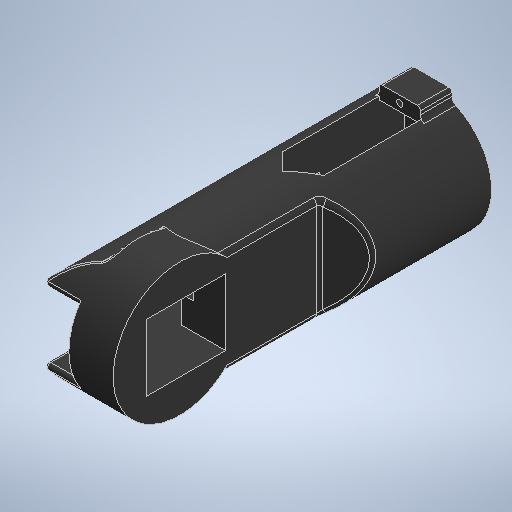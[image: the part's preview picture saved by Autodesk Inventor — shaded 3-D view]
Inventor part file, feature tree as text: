
AUTODESK INVENTOR PART (.ipt)
format: ipt  version: 2025.1 (Build 291241020, 241B)  size: 562,688 bytes
history: native  units: mm
features: extrude x17, sketch x14, fillet x6, chamfer x1, plane x1
ambient origin geometry x8: Origin, YZ Plane, XZ Plane, XY Plane, X Axis, Y Axis, Z Axis, Center Point
bodies: Body1 (feature_tree)
feature tree (39):
  extrude  "Extrusion11"  Depth=111.0mm TaperAngle=0.0deg
  extrude  "Extrusion12"  Depth=2.0mm TaperAngle=0.0deg
  extrude  "Extrusion13"  Depth=37.0mm
  extrude  "Extrusion14"  TaperAngle=0.0deg  [1 undecoded]
  extrude  "Extrusion15"  Depth=13.0mm
  extrude  "Extrusion16"  Depth=8.0mm TaperAngle=0.0deg
  fillet  "Fillet5"  Radius=7.2mm
  fillet  "Fillet6"  Radius=2.0mm
  extrude  "Extrusion17"  TaperAngle=0.0deg  [1 undecoded]
  chamfer  "Chamfer3"  Distance=10.0mm
  plane  "Work Plane3"
  extrude  "Extrusion18"  Depth=2.0mm
  extrude  "Extrusion19"  Depth=2.0mm
  sketch  "Sketch25"  dims[d184=19.1mm d185=2.0mm]
  extrude  "Extrusion20"  Depth=6.5mm TaperAngle=45.0deg
  extrude  "Extrusion21"  Depth=8.5mm TaperAngle=0.0deg
  extrude  "Extrusion22"  TaperAngle=0.0deg  [1 undecoded]
  sketch  "Sketch27"  dims[d191=65.0mm d192=8.5mm d193=0.0mm]
  extrude  "Extrusion23"  TaperAngle=0.0deg  [1 undecoded]
  extrude  "Extrusion24"  Depth=14.0mm TaperAngle=0.0deg
  extrude  "Extrusion25"  Depth=21.0mm
  extrude  "Extrusion26"  TaperAngle=0.0deg  [1 undecoded]
  fillet  "Fillet7"  Radius=60.0mm
  fillet  "Fillet8"  Radius=25.0mm
  fillet  "Fillet10"  Radius=21.0mm
  extrude  "Extrusion27"  Depth=35.5mm
  fillet  "Fillet11"  [1 undecoded]
  sketch  "Sketch15"  dims[d158=38.0mm d159=111.0mm d160=0.0mm]
  sketch  "Sketch16"  dims[d161=16.0mm d162=2.0mm d163=0.0mm]
  sketch  "Sketch17"  dims[d164=13.0mm d165=37.0mm]
  sketch  "Sketch18"  dims[d166=10.0mm d167=0.0mm d168=0.0mm]
  sketch  "Sketch19"  dims[d169=23.0mm d170=13.0mm]
  sketch  "Sketch20"  dims[d171=12.8mm d172=8.0mm d173=0.0mm d174=7.2mm d175=2.0mm]
  sketch  "Sketch21"  dims[d176=8.5mm d177=0.0mm d178=0.0mm]
  sketch  "Sketch23"  dims[d179=4.5mm d180=10.0mm d181=0.0mm]
  sketch  "Sketch24"  dims[d182=1.0mm d183=2.0mm]
  sketch  "Sketch26"  dims[d186=0.0mm d187=0.0mm d188=6.5mm d189=2.0mm d190=45.0deg]
  sketch  "Sketch28"  dims[d194=23.6mm d195=0.0mm d196=0.0mm]
  sketch  "Sketch29"  dims[d197=42.0mm d198=0.0mm d199=0.0mm d200=14.0mm d201=0.0mm d204=21.0mm d205=0.0mm d206=0.0mm d207=60.0mm d208=25.0mm d209=21.0mm d210=35.5mm d211=0.0mm d212=0.0mm d213=2.6mm d214=3.5mm d215=10.0mm d217=4.0mm d218=7.0mm d219=4.0mm d220=0.0mm d221=7.0mm d222=0.0mm d223=16.0mm d224=9.5mm d225=7.0mm d226=0.0mm d227=2.0mm d228=1.0mm d230=1.0mm d231=29.0mm d232=14.0mm d233=13.0mm d234=10.0mm d235=0.0mm d236=2.0mm]
note: 6 required parameter values undecoded (feature->parameter linkage not recoverable at this tier; creation-order binding heuristic only, values carry confidence <= 0.55)
